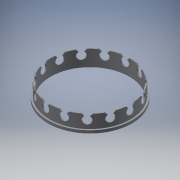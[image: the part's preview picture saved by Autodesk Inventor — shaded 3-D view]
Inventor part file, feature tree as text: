
AUTODESK INVENTOR PART (.ipt)
format: ipt  version: 2018 (Build 220112000, 112)  size: 279,552 bytes
history: native  units: in
note: dims shown in document units (in); Inventor stores cm internally (conversion verified against a paired STEP export)
features: extrude x5, sketch x5, mirror x1, pattern_circular x1, projected_geometry x1
ambient origin geometry x8: Origin, YZ Plane, XZ Plane, XY Plane, X Axis, Y Axis, Z Axis, Center Point
bodies: Solid1 (feature_tree)
feature tree (13):
  extrude  "Extrusion1"  Depth=3.57in
  extrude  "Extrusion2"  Depth=0.3in
  sketch  "Sketch3"  dims[d5=0.25in d6=3.0625in d7=0.0in]
  extrude  "Extrusion5"  Depth=0.25in TaperAngle=0.0deg
  mirror  "Mirror3"
  pattern_circular  "Circular Pattern1"  Angle=45.0deg  [1 undecoded]
  extrude  "Extrusion6"  Depth=0.125in
  extrude  "Extrusion8"  Depth=0.125in TaperAngle=360.0deg
  sketch  "Sketch1"  dims[d0=3.68in d1=3.57in]
  sketch  "Sketch2"  dims[d2=0.5in d3=0.0in d4=0.3in]
  sketch  "Sketch4"  dims[d8=0.35in]
  projected_geometry  "Projected Loop1"
  sketch  "Sketch6"  dims[d9=0.25in d11=45.0deg d14=0.0938in d17=5.9055in d18=360.0deg d21=0.08in d25=3.0625in d26=0.0in d27=0.1in d28=0.0in d32=3.875in d33=0.125in d34=0.0in]
note: 1 required parameter value undecoded (feature->parameter linkage not recoverable at this tier; creation-order binding heuristic only, values carry confidence <= 0.55)
